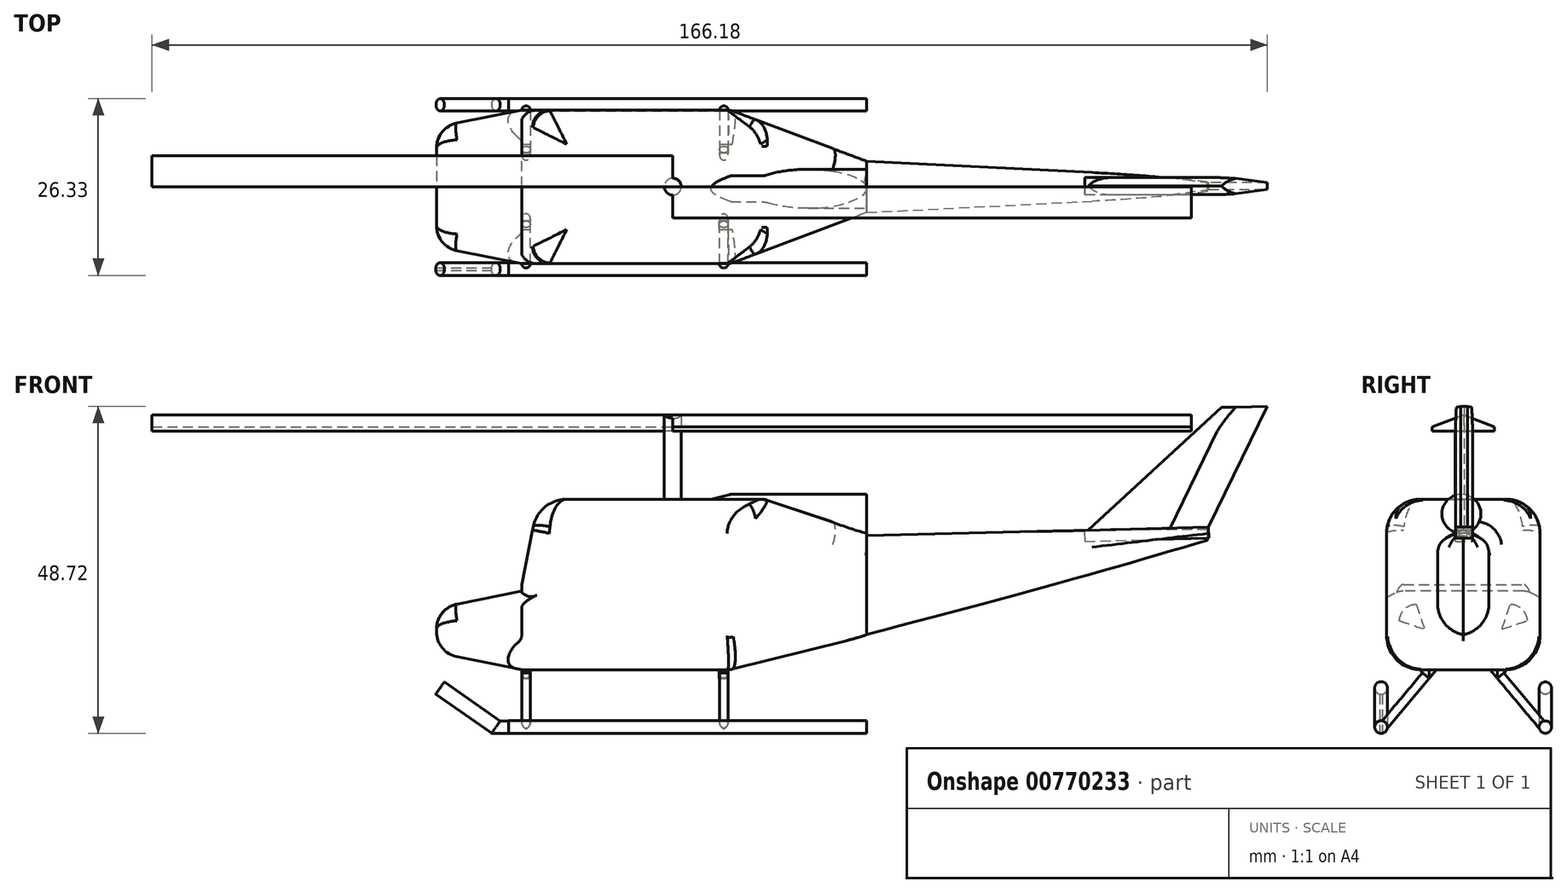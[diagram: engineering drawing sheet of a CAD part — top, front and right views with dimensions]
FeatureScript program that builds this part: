
annotation { "Feature Type Name" : "Feature", "Feature Type Description" : "" }
export const myFeature = defineFeature(function(context is Context, id is Id, definition is map)
    precondition{}
    {
        {
            var Q0;
            Q0=qCreatedBy(makeId("Top.planeOp"),FACE);
            var sketch = newSketch(context, id + "F0", { "sketchPlane" : qUnion([Q0])});
            skLineSegment(sketch, "E0.bottom", {"start": v(0, 0) * mm, "end": v(51.4, 0) * mm});
            skLineSegment(sketch, "E0.top", {"start": v(0, -22.87) * mm, "end": v(51.4, -22.87) * mm});
            skLineSegment(sketch, "E0.left", {"start": v(0, 0) * mm, "end": v(0, -22.87) * mm});
            skLineSegment(sketch, "E0.right", {"start": v(51.4, 0) * mm, "end": v(51.4, -22.87) * mm});
            skSolve(sketch);
        }
        {
            var Q0;
            Q0 = qSketchRegion(id + "F0", true);
            extrude(context, id + "F1", {"entities" : qUnion([Q0]), "depth" : 25.4 * mm, "offsetDistance" : 25.4 * mm});
        }
        {
            var Q0;
            Q0=makeQuery(id+"F1.opExtrude","SWEPT_FACE",FACE,{"disambiguationData":[OSD([sQuery(id+"F0.wireOp",EDGE,"E0.left")])]});
            var sketch = newSketch(context, id + "F2", { "sketchPlane" : qUnion([Q0])});
            skLineSegment(sketch, "E1.bottom", {"start": v(0, 0) * mm, "end": v(22.87, 0) * mm});
            skLineSegment(sketch, "E1.top", {"start": v(0, 11.7) * mm, "end": v(22.87, 11.7) * mm});
            skLineSegment(sketch, "E1.left", {"start": v(0, 0) * mm, "end": v(0, 11.7) * mm});
            skLineSegment(sketch, "E1.right", {"start": v(22.87, 0) * mm, "end": v(22.87, 11.7) * mm});
            skSolve(sketch);
        }
        {
            var Q0;
            Q0 = qSketchRegion(id + "F2", true);
            extrude(context, id + "F3", {"entities" : qUnion([Q0]), "operationType" : NewBodyOperationType.ADD, "depth" : 12.7 * mm, "offsetDistance" : 25.4 * mm});
        }
        {
            var Q0;
            Q0=makeQuery(id+"F1.opExtrude","CAP_EDGE",EDGE,{"disambiguationData":[OSD([sQuery(id+"F0.wireOp",EDGE,"E0.left")])],"isStart":false});
            chamfer(context, id + "F4", {"entities" : qUnion([Q0]), "chamferType" : ChamferType.TWO_OFFSETS, "width1" : 2.54 * mm, "oppositeDirection" : false, "width2" : 12.7 * mm, "tangentPropagation" : true});
        }
        {
            var Q0;
            Q0=makeQuery(id+"F3.opExtrude","CAP_EDGE",EDGE,{"disambiguationData":[OSD([sQuery(id+"F2.wireOp",EDGE,"E1.left")])],"isStart":false});
            var Q1;
            Q1=makeQuery(id+"F3.opExtrude","CAP_EDGE",EDGE,{"disambiguationData":[OSD([sQuery(id+"F2.wireOp",EDGE,"E1.top")])],"isStart":false});
            var Q2;
            Q2=makeQuery(id+"F3.opExtrude","CAP_EDGE",EDGE,{"disambiguationData":[OSD([sQuery(id+"F2.wireOp",EDGE,"E1.right")])],"isStart":false});
            var Q3;
            Q3=makeQuery(id+"F3.opExtrude","CAP_EDGE",EDGE,{"disambiguationData":[OSD([sQuery(id+"F2.wireOp",EDGE,"E1.bottom")])],"isStart":false});
            chamfer(context, id + "F5", {"entities" : qUnion([Q0, Q1, Q2, Q3]), "chamferType" : ChamferType.TWO_OFFSETS, "width1" : 2.54 * mm, "oppositeDirection" : false, "width2" : 12.7 * mm, "tangentPropagation" : true});
        }
        {
            var Q0;
            Q0=makeQuery(id+"F1.opExtrude","CAP_EDGE",EDGE,{"disambiguationData":[OSD([sQuery(id+"F0.wireOp",EDGE,"E0.right")])],"isStart":true});
            chamfer(context, id + "F6", {"entities" : qUnion([Q0]), "chamferType" : ChamferType.TWO_OFFSETS, "width1" : 20.32 * mm, "oppositeDirection" : false, "width2" : 5.08 * mm, "tangentPropagation" : true});
        }
        {
            var Q0;
            Q0=makeQuery(id+"F1.opExtrude","SWEPT_EDGE",EDGE,{"disambiguationData":[OSD([sQuery(id+"F0.wireOp",EDGE,"E0.top"),sQuery(id+"F0.wireOp",EDGE,"E0.right")])]});
            var Q1;
            Q1=makeQuery(id+"F1.opExtrude","SWEPT_EDGE",EDGE,{"disambiguationData":[OSD([sQuery(id+"F0.wireOp",EDGE,"E0.bottom"),sQuery(id+"F0.wireOp",EDGE,"E0.right")])]});
            chamfer(context, id + "F7", {"entities" : qUnion([Q0, Q1]), "chamferType" : ChamferType.TWO_OFFSETS, "width1" : 7.62 * mm, "oppositeDirection" : false, "width2" : 20.32 * mm, "tangentPropagation" : true});
        }
        {
            var Q0;
            Q0=makeQuery(id+"F1.opExtrude","CAP_EDGE",EDGE,{"disambiguationData":[OSD([sQuery(id+"F0.wireOp",EDGE,"E0.right")])],"isStart":false});
            chamfer(context, id + "F8", {"entities" : qUnion([Q0]), "chamferType" : ChamferType.TWO_OFFSETS, "width1" : 5.08 * mm, "oppositeDirection" : false, "width2" : 15.24 * mm, "tangentPropagation" : true});
        }
        {
            var Q0;
            Q0=makeQuery(id+"F1.opExtrude","SWEPT_FACE",FACE,{"disambiguationData":[OSD([sQuery(id+"F0.wireOp",EDGE,"E0.right")])]});
            var sketch = newSketch(context, id + "F9", { "sketchPlane" : qUnion([Q0])});
            skCircle(sketch, "E2", {"center": v(-11.72, 23.22) * mm, "radius": 2.9 * mm});
            skSolve(sketch);
        }
        {
            var Q0;
            Q0 = qSketchRegion(id + "F9", true);
            extrude(context, id + "F10", {"entities" : qUnion([Q0]), "operationType" : NewBodyOperationType.ADD, "depth" : -25.4 * mm, "offsetDistance" : 25.4 * mm});
        }
        {
            var Q0;
            Q0=makeQuery(id+"F10.opExtrude","CAP_EDGE",EDGE,{"disambiguationData":[OSD([sQuery(id+"F9.wireOp",EDGE,"E2")])],"isStart":false});
            chamfer(context, id + "F11", {"entities" : qUnion([Q0]), "chamferType" : ChamferType.TWO_OFFSETS, "width1" : 5.08 * mm, "oppositeDirection" : false, "width2" : 1.27 * mm, "tangentPropagation" : true});
        }
        {
            var Q0;
            {var subQ0=sQuery(id+"F9.wireOp",EDGE,"E2");Q0=makeQuery(id+"F11.opChamfer","BLEND_EDGE",EDGE,{"blendedFrom":[makeQuery(id+"F10.opExtrude","CAP_EDGE",EDGE,{"disambiguationData":[OSD([subQ0])],"isStart":false}),makeQuery(id+"F10.opExtrude","SWEPT_FACE",FACE,{"disambiguationData":[OSD([subQ0])]})],"blendedInto":[makeQuery(id+"F10.opExtrude","SWEPT_FACE",FACE,{"disambiguationData":[OSD([subQ0])]})]});}
            var Q1;
            {var subQ0=sQuery(id+"F9.wireOp",EDGE,"E2");Q1=makeQuery(id+"F11.opChamfer","BLEND_EDGE",EDGE,{"blendedFrom":[makeQuery(id+"F10.opExtrude","CAP_EDGE",EDGE,{"disambiguationData":[OSD([subQ0])],"isStart":false}),makeQuery(id+"F10.opExtrude","CAP_FACE",FACE,{"disambiguationData":[OSD([subQ0])],"isStart":false})],"blendedInto":[makeQuery(id+"F10.opExtrude","CAP_FACE",FACE,{"disambiguationData":[OSD([subQ0])],"isStart":false})]});}
            fillet(context, id + "F12", {"entities" : qUnion([Q0, Q1]), "radius" : 0.76 * mm, "tangentPropagation" : true, "allowEdgeOverflow" : false});
        }
        {
            var Q0;
            {var subQ0=sQuery(id+"F0.wireOp",EDGE,"E0.right");Q0=makeQuery(id+"F7.opChamfer","BLEND_EDGE",EDGE,{"blendedFrom":[makeQuery(id+"F1.opExtrude","SWEPT_EDGE",EDGE,{"disambiguationData":[OSD([sQuery(id+"F0.wireOp",EDGE,"E0.bottom"),subQ0])]}),makeQuery(id+"F6.opChamfer","BLEND_FACE",FACE,{"disambiguationData":[OSD([subQ0])]})],"blendedInto":[makeQuery(id+"F6.opChamfer","BLEND_FACE",FACE,{"disambiguationData":[OSD([subQ0])]})]});}
            var Q1;
            {var subQ0=sQuery(id+"F0.wireOp",EDGE,"E0.right");var subQ1=sQuery(id+"F0.wireOp",EDGE,"E0.bottom");Q1=makeQuery(id+"F7.opChamfer","BLEND_EDGE",EDGE,{"blendedFrom":[makeQuery(id+"F1.opExtrude","SWEPT_EDGE",EDGE,{"disambiguationData":[OSD([subQ1,subQ0])]}),makeQuery(id+"F3.boolean.opBoolean","MERGE",FACE,{"derivedFrom":[makeQuery(id+"F1.opExtrude","CAP_FACE",FACE,{"disambiguationData":[OSD([subQ1,sQuery(id+"F0.wireOp",EDGE,"E0.top"),sQuery(id+"F0.wireOp",EDGE,"E0.left"),subQ0])],"isStart":true}),makeQuery(id+"F3.opExtrude","SWEPT_FACE",FACE,{"disambiguationData":[OSD([sQuery(id+"F2.wireOp",EDGE,"E1.bottom")])]})]})],"blendedInto":[makeQuery(id+"F3.boolean.opBoolean","MERGE",FACE,{"derivedFrom":[makeQuery(id+"F1.opExtrude","CAP_FACE",FACE,{"disambiguationData":[OSD([subQ1,sQuery(id+"F0.wireOp",EDGE,"E0.top"),sQuery(id+"F0.wireOp",EDGE,"E0.left"),subQ0])],"isStart":true}),makeQuery(id+"F3.opExtrude","SWEPT_FACE",FACE,{"disambiguationData":[OSD([sQuery(id+"F2.wireOp",EDGE,"E1.bottom")])]})]})]});}
            var Q2;
            Q2=makeQuery(id+"F3.boolean.opBoolean","MERGE",EDGE,{"derivedFrom":[makeQuery(id+"F1.opExtrude","CAP_EDGE",EDGE,{"disambiguationData":[OSD([sQuery(id+"F0.wireOp",EDGE,"E0.bottom")])],"isStart":true}),makeQuery(id+"F3.opExtrude","SWEPT_EDGE",EDGE,{"disambiguationData":[OSD([sQuery(id+"F2.wireOp",EDGE,"E1.bottom"),sQuery(id+"F2.wireOp",EDGE,"E1.left")])]})]});
            var Q3;
            Q3=makeQuery(id+"F3.boolean.opBoolean","MERGE",EDGE,{"derivedFrom":[makeQuery(id+"F1.opExtrude","CAP_EDGE",EDGE,{"disambiguationData":[OSD([sQuery(id+"F0.wireOp",EDGE,"E0.top")])],"isStart":true}),makeQuery(id+"F3.opExtrude","SWEPT_EDGE",EDGE,{"disambiguationData":[OSD([sQuery(id+"F2.wireOp",EDGE,"E1.bottom"),sQuery(id+"F2.wireOp",EDGE,"E1.right")])]})]});
            var Q4;
            {var subQ0=sQuery(id+"F0.wireOp",EDGE,"E0.right");var subQ1=sQuery(id+"F0.wireOp",EDGE,"E0.top");Q4=makeQuery(id+"F7.opChamfer","BLEND_EDGE",EDGE,{"blendedFrom":[makeQuery(id+"F1.opExtrude","SWEPT_EDGE",EDGE,{"disambiguationData":[OSD([subQ1,subQ0])]}),makeQuery(id+"F3.boolean.opBoolean","MERGE",FACE,{"derivedFrom":[makeQuery(id+"F1.opExtrude","CAP_FACE",FACE,{"disambiguationData":[OSD([sQuery(id+"F0.wireOp",EDGE,"E0.bottom"),subQ1,sQuery(id+"F0.wireOp",EDGE,"E0.left"),subQ0])],"isStart":true}),makeQuery(id+"F3.opExtrude","SWEPT_FACE",FACE,{"disambiguationData":[OSD([sQuery(id+"F2.wireOp",EDGE,"E1.bottom")])]})]})],"blendedInto":[makeQuery(id+"F3.boolean.opBoolean","MERGE",FACE,{"derivedFrom":[makeQuery(id+"F1.opExtrude","CAP_FACE",FACE,{"disambiguationData":[OSD([sQuery(id+"F0.wireOp",EDGE,"E0.bottom"),subQ1,sQuery(id+"F0.wireOp",EDGE,"E0.left"),subQ0])],"isStart":true}),makeQuery(id+"F3.opExtrude","SWEPT_FACE",FACE,{"disambiguationData":[OSD([sQuery(id+"F2.wireOp",EDGE,"E1.bottom")])]})]})]});}
            var Q5;
            {var subQ0=sQuery(id+"F0.wireOp",EDGE,"E0.right");Q5=makeQuery(id+"F7.opChamfer","BLEND_EDGE",EDGE,{"blendedFrom":[makeQuery(id+"F1.opExtrude","SWEPT_EDGE",EDGE,{"disambiguationData":[OSD([sQuery(id+"F0.wireOp",EDGE,"E0.top"),subQ0])]}),makeQuery(id+"F6.opChamfer","BLEND_FACE",FACE,{"disambiguationData":[OSD([subQ0])]})],"blendedInto":[makeQuery(id+"F6.opChamfer","BLEND_FACE",FACE,{"disambiguationData":[OSD([subQ0])]})]});}
            fillet(context, id + "F13", {"entities" : qUnion([Q0, Q1, Q2, Q3, Q4, Q5]), "radius" : 5.08 * mm, "tangentPropagation" : true, "allowEdgeOverflow" : false});
        }
        {
            var Q0;
            {var subQ0=sQuery(id+"F2.wireOp",EDGE,"E1.top");Q0=makeQuery(id+"F5.opChamfer","BLEND_EDGE",EDGE,{"blendedFrom":[makeQuery(id+"F3.opExtrude","CAP_EDGE",EDGE,{"disambiguationData":[OSD([subQ0])],"isStart":false}),makeQuery(id+"F3.opExtrude","CAP_FACE",FACE,{"disambiguationData":[OSD([sQuery(id+"F2.wireOp",EDGE,"E1.bottom"),subQ0,sQuery(id+"F2.wireOp",EDGE,"E1.left"),sQuery(id+"F2.wireOp",EDGE,"E1.right")])],"isStart":false})],"blendedInto":[makeQuery(id+"F3.opExtrude","CAP_FACE",FACE,{"disambiguationData":[OSD([sQuery(id+"F2.wireOp",EDGE,"E1.bottom"),subQ0,sQuery(id+"F2.wireOp",EDGE,"E1.left"),sQuery(id+"F2.wireOp",EDGE,"E1.right")])],"isStart":false})]});}
            var Q1;
            {var subQ0=sQuery(id+"F2.wireOp",EDGE,"E1.right");Q1=makeQuery(id+"F5.opChamfer","BLEND_EDGE",EDGE,{"blendedFrom":[makeQuery(id+"F3.opExtrude","CAP_EDGE",EDGE,{"disambiguationData":[OSD([subQ0])],"isStart":false}),makeQuery(id+"F3.opExtrude","CAP_FACE",FACE,{"disambiguationData":[OSD([sQuery(id+"F2.wireOp",EDGE,"E1.bottom"),sQuery(id+"F2.wireOp",EDGE,"E1.top"),sQuery(id+"F2.wireOp",EDGE,"E1.left"),subQ0])],"isStart":false})],"blendedInto":[makeQuery(id+"F3.opExtrude","CAP_FACE",FACE,{"disambiguationData":[OSD([sQuery(id+"F2.wireOp",EDGE,"E1.bottom"),sQuery(id+"F2.wireOp",EDGE,"E1.top"),sQuery(id+"F2.wireOp",EDGE,"E1.left"),subQ0])],"isStart":false})]});}
            var Q2;
            {var subQ0=sQuery(id+"F2.wireOp",EDGE,"E1.bottom");Q2=makeQuery(id+"F5.opChamfer","BLEND_EDGE",EDGE,{"blendedFrom":[makeQuery(id+"F3.opExtrude","CAP_EDGE",EDGE,{"disambiguationData":[OSD([subQ0])],"isStart":false}),makeQuery(id+"F3.opExtrude","CAP_FACE",FACE,{"disambiguationData":[OSD([subQ0,sQuery(id+"F2.wireOp",EDGE,"E1.top"),sQuery(id+"F2.wireOp",EDGE,"E1.left"),sQuery(id+"F2.wireOp",EDGE,"E1.right")])],"isStart":false})],"blendedInto":[makeQuery(id+"F3.opExtrude","CAP_FACE",FACE,{"disambiguationData":[OSD([subQ0,sQuery(id+"F2.wireOp",EDGE,"E1.top"),sQuery(id+"F2.wireOp",EDGE,"E1.left"),sQuery(id+"F2.wireOp",EDGE,"E1.right")])],"isStart":false})]});}
            var Q3;
            {var subQ0=sQuery(id+"F2.wireOp",EDGE,"E1.left");Q3=makeQuery(id+"F5.opChamfer","BLEND_EDGE",EDGE,{"blendedFrom":[makeQuery(id+"F3.opExtrude","CAP_EDGE",EDGE,{"disambiguationData":[OSD([subQ0])],"isStart":false}),makeQuery(id+"F3.opExtrude","CAP_FACE",FACE,{"disambiguationData":[OSD([sQuery(id+"F2.wireOp",EDGE,"E1.bottom"),sQuery(id+"F2.wireOp",EDGE,"E1.top"),subQ0,sQuery(id+"F2.wireOp",EDGE,"E1.right")])],"isStart":false})],"blendedInto":[makeQuery(id+"F3.opExtrude","CAP_FACE",FACE,{"disambiguationData":[OSD([sQuery(id+"F2.wireOp",EDGE,"E1.bottom"),sQuery(id+"F2.wireOp",EDGE,"E1.top"),subQ0,sQuery(id+"F2.wireOp",EDGE,"E1.right")])],"isStart":false})]});}
            var Q4;
            Q4=makeQuery(id+"F5.opChamfer","BLEND_EDGE",EDGE,{"blendedFrom":[makeQuery(id+"F3.opExtrude","CAP_EDGE",EDGE,{"disambiguationData":[OSD([sQuery(id+"F2.wireOp",EDGE,"E1.bottom")])],"isStart":false}),makeQuery(id+"F3.opExtrude","CAP_EDGE",EDGE,{"disambiguationData":[OSD([sQuery(id+"F2.wireOp",EDGE,"E1.left")])],"isStart":false})],"blendedInto":[]});
            var Q5;
            Q5=makeQuery(id+"F5.opChamfer","BLEND_EDGE",EDGE,{"blendedFrom":[makeQuery(id+"F3.opExtrude","CAP_EDGE",EDGE,{"disambiguationData":[OSD([sQuery(id+"F2.wireOp",EDGE,"E1.bottom")])],"isStart":false}),makeQuery(id+"F3.opExtrude","CAP_EDGE",EDGE,{"disambiguationData":[OSD([sQuery(id+"F2.wireOp",EDGE,"E1.right")])],"isStart":false})],"blendedInto":[]});
            fillet(context, id + "F14", {"entities" : qUnion([Q0, Q1, Q2, Q3, Q4, Q5]), "radius" : 3.8 * mm, "tangentPropagation" : true, "allowEdgeOverflow" : false});
        }
        {
            var Q0;
            Q0=makeQuery(id+"F5.opChamfer","BLEND_EDGE",EDGE,{"blendedFrom":[makeQuery(id+"F3.opExtrude","CAP_EDGE",EDGE,{"disambiguationData":[OSD([sQuery(id+"F2.wireOp",EDGE,"E1.top")])],"isStart":false}),makeQuery(id+"F3.opExtrude","CAP_EDGE",EDGE,{"disambiguationData":[OSD([sQuery(id+"F2.wireOp",EDGE,"E1.left")])],"isStart":false})],"blendedInto":[]});
            var Q1;
            Q1=makeQuery(id+"F5.opChamfer","BLEND_EDGE",EDGE,{"blendedFrom":[makeQuery(id+"F3.opExtrude","CAP_EDGE",EDGE,{"disambiguationData":[OSD([sQuery(id+"F2.wireOp",EDGE,"E1.top")])],"isStart":false}),makeQuery(id+"F3.opExtrude","CAP_EDGE",EDGE,{"disambiguationData":[OSD([sQuery(id+"F2.wireOp",EDGE,"E1.right")])],"isStart":false})],"blendedInto":[]});
            fillet(context, id + "F15", {"entities" : qUnion([Q0, Q1]), "radius" : 2.54 * mm, "tangentPropagation" : true, "allowEdgeOverflow" : false});
        }
        {
            var Q0;
            Q0=makeQuery(id+"F4.opChamfer","BLEND_EDGE",EDGE,{"blendedFrom":[makeQuery(id+"F1.opExtrude","CAP_EDGE",EDGE,{"disambiguationData":[OSD([sQuery(id+"F0.wireOp",EDGE,"E0.left")])],"isStart":false}),makeQuery(id+"F3.boolean.opBoolean","MERGE",FACE,{"derivedFrom":[makeQuery(id+"F1.opExtrude","SWEPT_FACE",FACE,{"disambiguationData":[OSD([sQuery(id+"F0.wireOp",EDGE,"E0.bottom")])]}),makeQuery(id+"F3.opExtrude","SWEPT_FACE",FACE,{"disambiguationData":[OSD([sQuery(id+"F2.wireOp",EDGE,"E1.left")])]})]})],"blendedInto":[makeQuery(id+"F3.boolean.opBoolean","MERGE",FACE,{"derivedFrom":[makeQuery(id+"F1.opExtrude","SWEPT_FACE",FACE,{"disambiguationData":[OSD([sQuery(id+"F0.wireOp",EDGE,"E0.bottom")])]}),makeQuery(id+"F3.opExtrude","SWEPT_FACE",FACE,{"disambiguationData":[OSD([sQuery(id+"F2.wireOp",EDGE,"E1.left")])]})]})]});
            var Q1;
            Q1=makeQuery(id+"F4.opChamfer","BLEND_EDGE",EDGE,{"blendedFrom":[makeQuery(id+"F1.opExtrude","CAP_EDGE",EDGE,{"disambiguationData":[OSD([sQuery(id+"F0.wireOp",EDGE,"E0.left")])],"isStart":false}),makeQuery(id+"F3.boolean.opBoolean","MERGE",FACE,{"derivedFrom":[makeQuery(id+"F1.opExtrude","SWEPT_FACE",FACE,{"disambiguationData":[OSD([sQuery(id+"F0.wireOp",EDGE,"E0.top")])]}),makeQuery(id+"F3.opExtrude","SWEPT_FACE",FACE,{"disambiguationData":[OSD([sQuery(id+"F2.wireOp",EDGE,"E1.right")])]})]})],"blendedInto":[makeQuery(id+"F3.boolean.opBoolean","MERGE",FACE,{"derivedFrom":[makeQuery(id+"F1.opExtrude","SWEPT_FACE",FACE,{"disambiguationData":[OSD([sQuery(id+"F0.wireOp",EDGE,"E0.top")])]}),makeQuery(id+"F3.opExtrude","SWEPT_FACE",FACE,{"disambiguationData":[OSD([sQuery(id+"F2.wireOp",EDGE,"E1.right")])]})]})]});
            fillet(context, id + "F16", {"entities" : qUnion([Q0, Q1]), "radius" : 2.54 * mm, "tangentPropagation" : true, "allowEdgeOverflow" : false});
        }
        {
            var Q0;
            {var subQ0=sQuery(id+"F0.wireOp",EDGE,"E0.left");Q0=makeQuery(id+"F4.opChamfer","BLEND_EDGE",EDGE,{"blendedFrom":[makeQuery(id+"F1.opExtrude","CAP_EDGE",EDGE,{"disambiguationData":[OSD([subQ0])],"isStart":false}),makeQuery(id+"F1.opExtrude","CAP_FACE",FACE,{"disambiguationData":[OSD([sQuery(id+"F0.wireOp",EDGE,"E0.bottom"),sQuery(id+"F0.wireOp",EDGE,"E0.top"),subQ0,sQuery(id+"F0.wireOp",EDGE,"E0.right")])],"isStart":false})],"blendedInto":[makeQuery(id+"F1.opExtrude","CAP_FACE",FACE,{"disambiguationData":[OSD([sQuery(id+"F0.wireOp",EDGE,"E0.bottom"),sQuery(id+"F0.wireOp",EDGE,"E0.top"),subQ0,sQuery(id+"F0.wireOp",EDGE,"E0.right")])],"isStart":false})]});}
            fillet(context, id + "F17", {"entities" : qUnion([Q0]), "radius" : 5.08 * mm, "tangentPropagation" : true, "allowEdgeOverflow" : false});
        }
        {
            var Q0;
            {var subQ0=sQuery(id+"F0.wireOp",EDGE,"E0.right");Q0=makeQuery(id+"F8.opChamfer","BLEND_EDGE",EDGE,{"blendedFrom":[makeQuery(id+"F1.opExtrude","CAP_EDGE",EDGE,{"disambiguationData":[OSD([subQ0])],"isStart":false}),makeQuery(id+"F7.opChamfer","BLEND_FACE",FACE,{"disambiguationData":[OSD([sQuery(id+"F0.wireOp",EDGE,"E0.bottom"),subQ0])]})],"blendedInto":[makeQuery(id+"F7.opChamfer","BLEND_FACE",FACE,{"disambiguationData":[OSD([sQuery(id+"F0.wireOp",EDGE,"E0.bottom"),subQ0])]})]});}
            var Q1;
            {var subQ0=sQuery(id+"F0.wireOp",EDGE,"E0.right");Q1=makeQuery(id+"F8.opChamfer","BLEND_EDGE",EDGE,{"blendedFrom":[makeQuery(id+"F1.opExtrude","CAP_EDGE",EDGE,{"disambiguationData":[OSD([subQ0])],"isStart":false}),makeQuery(id+"F7.opChamfer","BLEND_FACE",FACE,{"disambiguationData":[OSD([sQuery(id+"F0.wireOp",EDGE,"E0.top"),subQ0])]})],"blendedInto":[makeQuery(id+"F7.opChamfer","BLEND_FACE",FACE,{"disambiguationData":[OSD([sQuery(id+"F0.wireOp",EDGE,"E0.top"),subQ0])]})]});}
            fillet(context, id + "F18", {"entities" : qUnion([Q0, Q1]), "radius" : 3.56 * mm, "tangentPropagation" : true, "allowEdgeOverflow" : false});
        }
        {
            var Q0;
            {var subQ0=sQuery(id+"F0.wireOp",EDGE,"E0.right");var subQ1=sQuery(id+"F0.wireOp",EDGE,"E0.bottom");var subQ2=makeQuery(id+"F1.opExtrude","CAP_FACE",FACE,{"disambiguationData":[OSD([subQ1,sQuery(id+"F0.wireOp",EDGE,"E0.top"),sQuery(id+"F0.wireOp",EDGE,"E0.left"),subQ0])],"isStart":false});Q0=makeQuery(id+"F10.boolean.opBoolean","SPLIT",EDGE,{"disambiguationData":[TD([makeQuery(id+"F7.opChamfer","BLEND_FACE",FACE,{"disambiguationData":[OSD([subQ1,subQ0])]})])],"derivedFrom":makeQuery(id+"F8.opChamfer","BLEND_EDGE",EDGE,{"blendedFrom":[makeQuery(id+"F1.opExtrude","CAP_EDGE",EDGE,{"disambiguationData":[OSD([subQ0])],"isStart":false}),subQ2],"blendedInto":[subQ2]})});}
            var Q1;
            {var subQ0=sQuery(id+"F0.wireOp",EDGE,"E0.right");var subQ1=sQuery(id+"F0.wireOp",EDGE,"E0.top");var subQ2=makeQuery(id+"F1.opExtrude","CAP_FACE",FACE,{"disambiguationData":[OSD([sQuery(id+"F0.wireOp",EDGE,"E0.bottom"),subQ1,sQuery(id+"F0.wireOp",EDGE,"E0.left"),subQ0])],"isStart":false});Q1=makeQuery(id+"F10.boolean.opBoolean","SPLIT",EDGE,{"disambiguationData":[TD([makeQuery(id+"F7.opChamfer","BLEND_FACE",FACE,{"disambiguationData":[OSD([subQ1,subQ0])]})])],"derivedFrom":makeQuery(id+"F8.opChamfer","BLEND_EDGE",EDGE,{"blendedFrom":[makeQuery(id+"F1.opExtrude","CAP_EDGE",EDGE,{"disambiguationData":[OSD([subQ0])],"isStart":false}),subQ2],"blendedInto":[subQ2]})});}
            fillet(context, id + "F19", {"entities" : qUnion([Q0, Q1]), "radius" : 2.54 * mm, "tangentPropagation" : true, "allowEdgeOverflow" : false});
        }
        {
            var Q0;
            Q0=makeQuery(id+"F1.opExtrude","SWEPT_FACE",FACE,{"disambiguationData":[OSD([sQuery(id+"F0.wireOp",EDGE,"E0.right")])]});
            var sketch = newSketch(context, id + "F20", { "sketchPlane" : qUnion([Q0])});
            skLineSegment(sketch, "E3.bottom", {"start": v(-7.62, 5.2) * mm, "end": v(-15.25, 5.2) * mm});
            skLineSegment(sketch, "E3.top", {"start": v(-7.62, 21.22) * mm, "end": v(-15.25, 21.22) * mm});
            skLineSegment(sketch, "E3.left", {"start": v(-7.62, 5.2) * mm, "end": v(-7.62, 21.22) * mm});
            skLineSegment(sketch, "E3.right", {"start": v(-15.25, 5.2) * mm, "end": v(-15.25, 21.22) * mm});
            skSolve(sketch);
        }
        {
            var Q0;
            Q0 = qSketchRegion(id + "F20", true);
            extrude(context, id + "F21", {"entities" : qUnion([Q0]), "depth" : 50.8 * mm, "offsetDistance" : 25.4 * mm});
        }
        {
            var Q0;
            Q0=makeQuery(id+"F21.opExtrude","CAP_EDGE",EDGE,{"disambiguationData":[OSD([sQuery(id+"F20.wireOp",EDGE,"E3.bottom")])],"isStart":false});
            chamfer(context, id + "F22", {"entities" : qUnion([Q0]), "chamferType" : ChamferType.TWO_OFFSETS, "width1" : 50.8 * mm, "oppositeDirection" : false, "width2" : 12.7 * mm, "tangentPropagation" : true});
        }
        {
            var Q0;
            Q0=makeQuery(id+"F21.opExtrude","CAP_EDGE",EDGE,{"disambiguationData":[OSD([sQuery(id+"F20.wireOp",EDGE,"E3.top")])],"isStart":true});
            chamfer(context, id + "F23", {"entities" : qUnion([Q0]), "chamferType" : ChamferType.TWO_OFFSETS, "width1" : 50.8 * mm, "oppositeDirection" : false, "width2" : 1.27 * mm, "tangentPropagation" : true});
        }
        {
            var Q0;
            Q0=makeQuery(id+"F21.opExtrude","CAP_EDGE",EDGE,{"disambiguationData":[OSD([sQuery(id+"F20.wireOp",EDGE,"E3.right")])],"isStart":false});
            var Q1;
            Q1=makeQuery(id+"F21.opExtrude","CAP_EDGE",EDGE,{"disambiguationData":[OSD([sQuery(id+"F20.wireOp",EDGE,"E3.left")])],"isStart":false});
            chamfer(context, id + "F24", {"entities" : qUnion([Q0, Q1]), "chamferType" : ChamferType.TWO_OFFSETS, "width1" : 50.8 * mm, "oppositeDirection" : false, "width2" : 2.54 * mm, "tangentPropagation" : true});
        }
        {
            var Q0;
            Q0=makeQuery(id+"F24.opChamfer","BLEND_EDGE",EDGE,{"blendedFrom":[makeQuery(id+"F21.opExtrude","CAP_EDGE",EDGE,{"disambiguationData":[OSD([sQuery(id+"F20.wireOp",EDGE,"E3.right")])],"isStart":false}),makeQuery(id+"F23.opChamfer","BLEND_FACE",FACE,{"disambiguationData":[OSD([sQuery(id+"F20.wireOp",EDGE,"E3.top")])]})],"blendedInto":[makeQuery(id+"F23.opChamfer","BLEND_FACE",FACE,{"disambiguationData":[OSD([sQuery(id+"F20.wireOp",EDGE,"E3.top")])]})]});
            var Q1;
            Q1=makeQuery(id+"F24.opChamfer","BLEND_EDGE",EDGE,{"blendedFrom":[makeQuery(id+"F21.opExtrude","CAP_EDGE",EDGE,{"disambiguationData":[OSD([sQuery(id+"F20.wireOp",EDGE,"E3.left")])],"isStart":false}),makeQuery(id+"F23.opChamfer","BLEND_FACE",FACE,{"disambiguationData":[OSD([sQuery(id+"F20.wireOp",EDGE,"E3.top")])]})],"blendedInto":[makeQuery(id+"F23.opChamfer","BLEND_FACE",FACE,{"disambiguationData":[OSD([sQuery(id+"F20.wireOp",EDGE,"E3.top")])]})]});
            fillet(context, id + "F25", {"entities" : qUnion([Q0, Q1]), "radius" : 2.54 * mm, "tangentPropagation" : true, "allowEdgeOverflow" : false});
        }
        {
            var Q0;
            Q0=makeQuery(id+"F24.opChamfer","BLEND_EDGE",EDGE,{"blendedFrom":[makeQuery(id+"F21.opExtrude","CAP_EDGE",EDGE,{"disambiguationData":[OSD([sQuery(id+"F20.wireOp",EDGE,"E3.right")])],"isStart":false}),makeQuery(id+"F22.opChamfer","BLEND_FACE",FACE,{"disambiguationData":[OSD([sQuery(id+"F20.wireOp",EDGE,"E3.bottom")])]})],"blendedInto":[makeQuery(id+"F22.opChamfer","BLEND_FACE",FACE,{"disambiguationData":[OSD([sQuery(id+"F20.wireOp",EDGE,"E3.bottom")])]})]});
            var Q1;
            Q1=makeQuery(id+"F24.opChamfer","BLEND_EDGE",EDGE,{"blendedFrom":[makeQuery(id+"F21.opExtrude","CAP_EDGE",EDGE,{"disambiguationData":[OSD([sQuery(id+"F20.wireOp",EDGE,"E3.left")])],"isStart":false}),makeQuery(id+"F22.opChamfer","BLEND_FACE",FACE,{"disambiguationData":[OSD([sQuery(id+"F20.wireOp",EDGE,"E3.bottom")])]})],"blendedInto":[makeQuery(id+"F22.opChamfer","BLEND_FACE",FACE,{"disambiguationData":[OSD([sQuery(id+"F20.wireOp",EDGE,"E3.bottom")])]})]});
            fillet(context, id + "F26", {"entities" : qUnion([Q0, Q1]), "radius" : 4.57 * mm, "tangentPropagation" : true, "allowEdgeOverflow" : false});
        }
        {
            var Q0;
            Q0=makeQuery(id+"F23.opChamfer","BLEND_FACE",FACE,{"disambiguationData":[OSD([sQuery(id+"F20.wireOp",EDGE,"E3.top")])]});
            var sketch = newSketch(context, id + "F27", { "sketchPlane" : qUnion([Q0])});
            skLineSegment(sketch, "E4.bottom", {"start": v(84.4, -12.6) * mm, "end": v(113.37, -12.6) * mm});
            skLineSegment(sketch, "E4.top", {"start": v(84.4, -10.05) * mm, "end": v(113.37, -10.05) * mm});
            skLineSegment(sketch, "E4.left", {"start": v(84.4, -12.6) * mm, "end": v(84.4, -10.05) * mm});
            skLineSegment(sketch, "E4.right", {"start": v(113.37, -12.6) * mm, "end": v(113.37, -10.05) * mm});
            skSolve(sketch);
        }
        {
            var Q0;
            Q0 = qSketchRegion(id + "F27", true);
            extrude(context, id + "F28", {"entities" : qUnion([Q0]), "depth" : 17.78 * mm, "offsetDistance" : 25.4 * mm});
        }
        {
            var Q0;
            Q0=makeQuery(id+"F28.opExtrude","CAP_EDGE",EDGE,{"disambiguationData":[OSD([sQuery(id+"F27.wireOp",EDGE,"E4.right")])],"isStart":true});
            chamfer(context, id + "F29", {"entities" : qUnion([Q0]), "chamferType" : ChamferType.TWO_OFFSETS, "width1" : 20.32 * mm, "oppositeDirection" : false, "width2" : 10.54 * mm, "tangentPropagation" : true});
        }
        {
            var Q0;
            Q0=makeQuery(id+"F28.opExtrude","CAP_EDGE",EDGE,{"disambiguationData":[OSD([sQuery(id+"F27.wireOp",EDGE,"E4.left")])],"isStart":false});
            chamfer(context, id + "F30", {"entities" : qUnion([Q0]), "chamferType" : ChamferType.TWO_OFFSETS, "width1" : 17.78 * mm, "oppositeDirection" : false, "width2" : 20.32 * mm, "tangentPropagation" : true});
        }
        {
            var Q0;
            Q0=makeQuery(id+"F28.opExtrude","CAP_FACE",FACE,{"disambiguationData":[OSD([sQuery(id+"F27.wireOp",EDGE,"E4.bottom"),sQuery(id+"F27.wireOp",EDGE,"E4.top"),sQuery(id+"F27.wireOp",EDGE,"E4.left"),sQuery(id+"F27.wireOp",EDGE,"E4.right")])],"isStart":true});
            extrude(context, id + "F31", {"entities" : qUnion([Q0]), "depth" : 1.65 * mm, "offsetDistance" : 25.4 * mm});
        }
        {
            var Q0;
            Q0=makeQuery(id+"F30.opChamfer","BLEND_EDGE",EDGE,{"blendedFrom":[makeQuery(id+"F28.opExtrude","CAP_EDGE",EDGE,{"disambiguationData":[OSD([sQuery(id+"F27.wireOp",EDGE,"E4.left")])],"isStart":false}),makeQuery(id+"F28.opExtrude","SWEPT_FACE",FACE,{"disambiguationData":[OSD([sQuery(id+"F27.wireOp",EDGE,"E4.top")])]})],"blendedInto":[makeQuery(id+"F28.opExtrude","SWEPT_FACE",FACE,{"disambiguationData":[OSD([sQuery(id+"F27.wireOp",EDGE,"E4.top")])]})]});
            var Q1;
            Q1=makeQuery(id+"F30.opChamfer","BLEND_EDGE",EDGE,{"blendedFrom":[makeQuery(id+"F28.opExtrude","CAP_EDGE",EDGE,{"disambiguationData":[OSD([sQuery(id+"F27.wireOp",EDGE,"E4.left")])],"isStart":false}),makeQuery(id+"F28.opExtrude","SWEPT_FACE",FACE,{"disambiguationData":[OSD([sQuery(id+"F27.wireOp",EDGE,"E4.bottom")])]})],"blendedInto":[makeQuery(id+"F28.opExtrude","SWEPT_FACE",FACE,{"disambiguationData":[OSD([sQuery(id+"F27.wireOp",EDGE,"E4.bottom")])]})]});
            fillet(context, id + "F32", {"entities" : qUnion([Q0, Q1]), "radius" : 2.54 * mm, "tangentPropagation" : true, "allowEdgeOverflow" : false});
        }
        {
            var Q0;
            Q0=makeQuery(id+"F29.opChamfer","BLEND_EDGE",EDGE,{"blendedFrom":[makeQuery(id+"F28.opExtrude","CAP_EDGE",EDGE,{"disambiguationData":[OSD([sQuery(id+"F27.wireOp",EDGE,"E4.right")])],"isStart":true}),makeQuery(id+"F28.opExtrude","SWEPT_FACE",FACE,{"disambiguationData":[OSD([sQuery(id+"F27.wireOp",EDGE,"E4.bottom")])]})],"blendedInto":[makeQuery(id+"F28.opExtrude","SWEPT_FACE",FACE,{"disambiguationData":[OSD([sQuery(id+"F27.wireOp",EDGE,"E4.bottom")])]})]});
            var Q1;
            Q1=makeQuery(id+"F29.opChamfer","BLEND_EDGE",EDGE,{"blendedFrom":[makeQuery(id+"F28.opExtrude","CAP_EDGE",EDGE,{"disambiguationData":[OSD([sQuery(id+"F27.wireOp",EDGE,"E4.right")])],"isStart":true}),makeQuery(id+"F28.opExtrude","SWEPT_FACE",FACE,{"disambiguationData":[OSD([sQuery(id+"F27.wireOp",EDGE,"E4.top")])]})],"blendedInto":[makeQuery(id+"F28.opExtrude","SWEPT_FACE",FACE,{"disambiguationData":[OSD([sQuery(id+"F27.wireOp",EDGE,"E4.top")])]})]});
            chamfer(context, id + "F33", {"entities" : qUnion([Q0, Q1]), "chamferType" : ChamferType.TWO_OFFSETS, "width1" : 5.08 * mm, "oppositeDirection" : false, "width2" : 0.76 * mm, "tangentPropagation" : true});
        }
        {
            var Q0;
            Q0=makeQuery(id+"F1.opExtrude","CAP_FACE",FACE,{"disambiguationData":[OSD([sQuery(id+"F0.wireOp",EDGE,"E0.bottom"),sQuery(id+"F0.wireOp",EDGE,"E0.top"),sQuery(id+"F0.wireOp",EDGE,"E0.left"),sQuery(id+"F0.wireOp",EDGE,"E0.right")])],"isStart":false});
            var sketch = newSketch(context, id + "F34", { "sketchPlane" : qUnion([Q0])});
            skCircle(sketch, "E5", {"center": v(22.51, -11.4) * mm, "radius": 1.26 * mm});
            skSolve(sketch);
        }
        {
            var Q0;
            Q0 = qSketchRegion(id + "F34", true);
            extrude(context, id + "F35", {"entities" : qUnion([Q0]), "operationType" : NewBodyOperationType.ADD, "depth" : 12.7 * mm, "offsetDistance" : 25.4 * mm});
        }
        {
            var Q0;
            Q0=makeQuery(id+"F3.boolean.opBoolean","MERGE",FACE,{"derivedFrom":[makeQuery(id+"F1.opExtrude","CAP_FACE",FACE,{"disambiguationData":[OSD([sQuery(id+"F0.wireOp",EDGE,"E0.bottom"),sQuery(id+"F0.wireOp",EDGE,"E0.top"),sQuery(id+"F0.wireOp",EDGE,"E0.left"),sQuery(id+"F0.wireOp",EDGE,"E0.right")])],"isStart":true}),makeQuery(id+"F3.opExtrude","SWEPT_FACE",FACE,{"disambiguationData":[OSD([sQuery(id+"F2.wireOp",EDGE,"E1.bottom")])]})]});
            var sketch = newSketch(context, id + "F36", { "sketchPlane" : qUnion([Q0])});
            skLineSegment(sketch, "E6.bottom", {"start": v(0, 17.8) * mm, "end": v(1.3, 17.8) * mm});
            skLineSegment(sketch, "E6.top", {"start": v(0, 16.5) * mm, "end": v(1.3, 16.5) * mm});
            skLineSegment(sketch, "E6.left", {"start": v(0, 17.8) * mm, "end": v(0, 16.5) * mm});
            skLineSegment(sketch, "E6.right", {"start": v(1.3, 17.8) * mm, "end": v(1.3, 16.5) * mm});
            skLineSegment(sketch, "E7.bottom", {"start": v(0, 5.08) * mm, "end": v(1.3, 5.08) * mm});
            skLineSegment(sketch, "E7.top", {"start": v(0, 6.38) * mm, "end": v(1.3, 6.38) * mm});
            skLineSegment(sketch, "E7.left", {"start": v(0, 5.08) * mm, "end": v(0, 6.38) * mm});
            skLineSegment(sketch, "E7.right", {"start": v(1.3, 5.08) * mm, "end": v(1.3, 6.38) * mm});
            skLineSegment(sketch, "E8.bottom", {"start": v(30.76, 17.8) * mm, "end": v(29.4, 17.8) * mm});
            skLineSegment(sketch, "E8.top", {"start": v(30.76, 16.5) * mm, "end": v(29.4, 16.5) * mm});
            skLineSegment(sketch, "E8.left", {"start": v(30.76, 17.8) * mm, "end": v(30.76, 16.5) * mm});
            skLineSegment(sketch, "E8.right", {"start": v(29.4, 17.8) * mm, "end": v(29.4, 16.5) * mm});
            skLineSegment(sketch, "E9.bottom", {"start": v(30.76, 5.08) * mm, "end": v(29.47, 5.08) * mm});
            skLineSegment(sketch, "E9.top", {"start": v(30.76, 6.39) * mm, "end": v(29.47, 6.39) * mm});
            skLineSegment(sketch, "E9.left", {"start": v(30.76, 5.08) * mm, "end": v(30.76, 6.39) * mm});
            skLineSegment(sketch, "E9.right", {"start": v(29.47, 5.08) * mm, "end": v(29.47, 6.39) * mm});
            skSolve(sketch);
        }
        {
            var Q0;
            Q0 = qSketchRegion(id + "F36", true);
            extrude(context, id + "F37", {"entities" : qUnion([Q0]), "operationType" : NewBodyOperationType.ADD, "depth" : 1.3 * mm, "offsetDistance" : 25.4 * mm});
        }
        {
            var Q0;
            Q0=makeQuery(id+"F37.opExtrude","CAP_EDGE",EDGE,{"disambiguationData":[OSD([sQuery(id+"F36.wireOp",EDGE,"E6.bottom")])],"isStart":false});
            var Q1;
            Q1=makeQuery(id+"F37.opExtrude","CAP_EDGE",EDGE,{"disambiguationData":[OSD([sQuery(id+"F36.wireOp",EDGE,"E8.bottom")])],"isStart":false});
            var Q2;
            Q2=makeQuery(id+"F37.opExtrude","CAP_EDGE",EDGE,{"disambiguationData":[OSD([sQuery(id+"F36.wireOp",EDGE,"E7.bottom")])],"isStart":false});
            var Q3;
            Q3=makeQuery(id+"F37.opExtrude","CAP_EDGE",EDGE,{"disambiguationData":[OSD([sQuery(id+"F36.wireOp",EDGE,"E9.bottom")])],"isStart":false});
            chamfer(context, id + "F38", {"entities" : qUnion([Q0, Q1, Q2, Q3]), "chamferType" : ChamferType.OFFSET_ANGLE, "width" : 1.3 * mm, "oppositeDirection" : false, "angle" : 40 * degree, "tangentPropagation" : true});
        }
        {
            var Q0;
            Q0=makeQuery(id+"F38.opChamfer","BLEND_FACE",FACE,{"disambiguationData":[OSD([sQuery(id+"F36.wireOp",EDGE,"E7.bottom")])]});
            var sketch = newSketch(context, id + "F39", { "sketchPlane" : qUnion([Q0])});
            skCircle(sketch, "E10", {"center": v(0.65, 5.07) * mm, "radius": 0.64 * mm});
            skPoint(sketch, "E10.centerSnap0", {"position": v(0.65, 4.03) * mm});
            skCircle(sketch, "E11", {"center": v(30.11, 5.07) * mm, "radius": 0.64 * mm});
            skPoint(sketch, "E11.centerSnap0", {"position": v(30.11, 4.7) * mm});
            skSolve(sketch);
        }
        {
            var Q0;
            Q0 = qSketchRegion(id + "F39", true);
            extrude(context, id + "F40", {"entities" : qUnion([Q0]), "operationType" : NewBodyOperationType.ADD, "depth" : 10.16 * mm, "offsetDistance" : 25.4 * mm});
        }
        {
            var Q0;
            Q0 = qSketchRegion(id + "F39", true);
            extrude(context, id + "F41", {"entities" : qUnion([Q0]), "operationType" : NewBodyOperationType.ADD, "depth" : -2.54 * mm, "offsetDistance" : 25.4 * mm});
        }
        {
            var Q0;
            Q0=makeQuery(id+"F38.opChamfer","BLEND_FACE",FACE,{"disambiguationData":[OSD([sQuery(id+"F36.wireOp",EDGE,"E8.bottom")])]});
            var sketch = newSketch(context, id + "F42", { "sketchPlane" : qUnion([Q0])});
            skCircle(sketch, "E12", {"center": v(30.1, 12.48) * mm, "radius": 0.65 * mm});
            skCircle(sketch, "E13", {"center": v(0.65, 12.47) * mm, "radius": 0.65 * mm});
            skSolve(sketch);
        }
        {
            var Q0;
            Q0 = qSketchRegion(id + "F42", true);
            extrude(context, id + "F43", {"entities" : qUnion([Q0]), "operationType" : NewBodyOperationType.ADD, "depth" : 10.16 * mm, "offsetDistance" : 25.4 * mm});
        }
        {
            var Q0;
            Q0 = qSketchRegion(id + "F42", true);
            extrude(context, id + "F44", {"entities" : qUnion([Q0]), "operationType" : NewBodyOperationType.ADD, "depth" : -2.54 * mm, "offsetDistance" : 25.4 * mm});
        }
        {
            var Q0;
            Q0=makeQuery(id+"F10.opExtrude","CAP_FACE",FACE,{"disambiguationData":[OSD([sQuery(id+"F9.wireOp",EDGE,"E2")])],"isStart":true});
            var sketch = newSketch(context, id + "F45", { "sketchPlane" : qUnion([Q0])});
            skCircle(sketch, "E14", {"center": v(-23.68, -8.55) * mm, "radius": 0.94 * mm});
            skCircle(sketch, "E15", {"center": v(0.8, -8.55) * mm, "radius": 0.92 * mm});
            skSolve(sketch);
        }
        {
            var Q0;
            Q0 = qSketchRegion(id + "F45", true);
            extrude(context, id + "F46", {"entities" : qUnion([Q0]), "operationType" : NewBodyOperationType.ADD, "depth" : -53.34 * mm, "offsetDistance" : 25.4 * mm});
        }
        {
            var Q0;
            Q0=makeQuery(id+"F46.opExtrude","CAP_FACE",FACE,{"disambiguationData":[OSD([sQuery(id+"F45.wireOp",EDGE,"E14")])],"isStart":false});
            var sketch = newSketch(context, id + "F47", { "sketchPlane" : qUnion([Q0])});
            skLineSegment(sketch, "E16.bottom", {"start": v(22.75, -9.48) * mm, "end": v(24.62, -9.48) * mm});
            skLineSegment(sketch, "E16.top", {"start": v(22.75, -7.62) * mm, "end": v(24.62, -7.62) * mm});
            skLineSegment(sketch, "E16.left", {"start": v(22.75, -9.48) * mm, "end": v(22.75, -7.62) * mm});
            skLineSegment(sketch, "E16.right", {"start": v(24.62, -9.48) * mm, "end": v(24.62, -7.62) * mm});
            skLineSegment(sketch, "E17.bottom", {"start": v(-1.7, -9.45) * mm, "end": v(0.11, -9.45) * mm});
            skLineSegment(sketch, "E17.top", {"start": v(-1.7, -7.65) * mm, "end": v(0.11, -7.65) * mm});
            skLineSegment(sketch, "E17.left", {"start": v(-1.7, -9.45) * mm, "end": v(-1.7, -7.65) * mm});
            skLineSegment(sketch, "E17.right", {"start": v(0.11, -9.45) * mm, "end": v(0.11, -7.65) * mm});
            skSolve(sketch);
        }
        {
            var Q0;
            Q0 = qSketchRegion(id + "F47", true);
            extrude(context, id + "F48", {"entities" : qUnion([Q0]), "operationType" : NewBodyOperationType.ADD, "depth" : 2.54 * mm, "offsetDistance" : 25.4 * mm});
        }
        {
            var Q0;
            Q0=makeQuery(id+"F48.opExtrude","CAP_EDGE",EDGE,{"disambiguationData":[OSD([sQuery(id+"F47.wireOp",EDGE,"E16.top")])],"isStart":false});
            var Q1;
            Q1=makeQuery(id+"F48.opExtrude","CAP_EDGE",EDGE,{"disambiguationData":[OSD([sQuery(id+"F47.wireOp",EDGE,"E17.top")])],"isStart":false});
            chamfer(context, id + "F49", {"entities" : qUnion([Q0, Q1]), "chamferType" : ChamferType.OFFSET_ANGLE, "width" : 1.3 * mm, "oppositeDirection" : false, "angle" : 55 * degree, "tangentPropagation" : true});
        }
        {
            var Q0;
            Q0=makeQuery(id+"F48.opExtrude","SWEPT_EDGE",EDGE,{"disambiguationData":[OSD([sQuery(id+"F47.wireOp",EDGE,"E17.top"),sQuery(id+"F47.wireOp",EDGE,"E17.left")])]});
            var Q1;
            Q1=makeQuery(id+"F48.opExtrude","SWEPT_EDGE",EDGE,{"disambiguationData":[OSD([sQuery(id+"F47.wireOp",EDGE,"E17.top"),sQuery(id+"F47.wireOp",EDGE,"E17.right")])]});
            var Q2;
            Q2=makeQuery(id+"F48.opExtrude","SWEPT_EDGE",EDGE,{"disambiguationData":[OSD([sQuery(id+"F47.wireOp",EDGE,"E17.bottom"),sQuery(id+"F47.wireOp",EDGE,"E17.right")])]});
            var Q3;
            Q3=makeQuery(id+"F48.opExtrude","SWEPT_EDGE",EDGE,{"disambiguationData":[OSD([sQuery(id+"F47.wireOp",EDGE,"E17.bottom"),sQuery(id+"F47.wireOp",EDGE,"E17.left")])]});
            var Q4;
            Q4=makeQuery(id+"F48.opExtrude","SWEPT_EDGE",EDGE,{"disambiguationData":[OSD([sQuery(id+"F47.wireOp",EDGE,"E16.bottom"),sQuery(id+"F47.wireOp",EDGE,"E16.right")])]});
            var Q5;
            Q5=makeQuery(id+"F48.opExtrude","SWEPT_EDGE",EDGE,{"disambiguationData":[OSD([sQuery(id+"F47.wireOp",EDGE,"E16.bottom"),sQuery(id+"F47.wireOp",EDGE,"E16.left")])]});
            var Q6;
            Q6=makeQuery(id+"F48.opExtrude","SWEPT_EDGE",EDGE,{"disambiguationData":[OSD([sQuery(id+"F47.wireOp",EDGE,"E16.top"),sQuery(id+"F47.wireOp",EDGE,"E16.right")])]});
            var Q7;
            Q7=makeQuery(id+"F48.opExtrude","SWEPT_EDGE",EDGE,{"disambiguationData":[OSD([sQuery(id+"F47.wireOp",EDGE,"E16.top"),sQuery(id+"F47.wireOp",EDGE,"E16.left")])]});
            fillet(context, id + "F50", {"entities" : qUnion([Q0, Q1, Q2, Q3, Q4, Q5, Q6, Q7]), "radius" : 0.89 * mm, "tangentPropagation" : true, "allowEdgeOverflow" : false});
        }
        {
            var Q0;
            Q0=makeQuery(id+"F49.opChamfer","BLEND_FACE",FACE,{"disambiguationData":[OSD([sQuery(id+"F47.wireOp",EDGE,"E16.top")])]});
            var Q1;
            Q1=makeQuery(id+"F49.opChamfer","BLEND_FACE",FACE,{"disambiguationData":[OSD([sQuery(id+"F47.wireOp",EDGE,"E17.top")])]});
            extrude(context, id + "F51", {"entities" : qUnion([Q0, Q1]), "operationType" : NewBodyOperationType.ADD, "depth" : 10.16 * mm, "offsetDistance" : 25.4 * mm});
        }
        {
            var Q0;
            {var subQ0=sQuery(id+"F47.wireOp",EDGE,"E16.right");var subQ1=sQuery(id+"F47.wireOp",EDGE,"E16.left");var subQ2=sQuery(id+"F47.wireOp",EDGE,"E16.top");var subQ3=sQuery(id+"F47.wireOp",EDGE,"E16.bottom");Q0=makeQuery(id+"F51.boolean.opBoolean","MERGE",EDGE,{"derivedFrom":[makeQuery(id+"F49.opChamfer","BLEND_EDGE",EDGE,{"blendedFrom":[makeQuery(id+"F48.opExtrude","CAP_EDGE",EDGE,{"disambiguationData":[OSD([subQ2])],"isStart":false}),makeQuery(id+"F48.opExtrude","CAP_FACE",FACE,{"disambiguationData":[OSD([subQ3,subQ2,subQ1,subQ0])],"isStart":false})],"blendedInto":[makeQuery(id+"F48.opExtrude","CAP_FACE",FACE,{"disambiguationData":[OSD([subQ3,subQ2,subQ1,subQ0])],"isStart":false})]}),makeQuery(id+"F51.opExtrude","CAP_EDGE",EDGE,{"disambiguationData":[OSD([subQ3,subQ2,subQ1,subQ0])],"isStart":true})]});}
            fillet(context, id + "F52", {"entities" : qUnion([Q0]), "radius" : 5.08 * mm, "tangentPropagation" : true, "allowEdgeOverflow" : false});
        }
        {
            var Q0;
            Q0=makeQuery(id+"F35.opExtrude","CAP_FACE",FACE,{"disambiguationData":[OSD([sQuery(id+"F34.wireOp",EDGE,"E5")])],"isStart":false});
            var sketch = newSketch(context, id + "F53", { "sketchPlane" : qUnion([Q0])});
            skLineSegment(sketch, "E18.bottom", {"start": v(22.51, -11.4) * mm, "end": v(99.8, -11.4) * mm});
            skLineSegment(sketch, "E18.top", {"start": v(22.51, -16.1) * mm, "end": v(99.8, -16.1) * mm});
            skLineSegment(sketch, "E18.left", {"start": v(22.51, -11.4) * mm, "end": v(22.51, -16.1) * mm});
            skLineSegment(sketch, "E18.right", {"start": v(99.8, -11.4) * mm, "end": v(99.8, -16.1) * mm});
            skLineSegment(sketch, "E19.bottom", {"start": v(22.51, -11.4) * mm, "end": v(-55.07, -11.4) * mm});
            skLineSegment(sketch, "E19.top", {"start": v(22.51, -6.8) * mm, "end": v(-55.07, -6.8) * mm});
            skLineSegment(sketch, "E19.left", {"start": v(22.51, -11.4) * mm, "end": v(22.51, -6.8) * mm});
            skLineSegment(sketch, "E19.right", {"start": v(-55.07, -11.4) * mm, "end": v(-55.07, -6.8) * mm});
            skSolve(sketch);
        }
        {
            var Q0;
            Q0 = qSketchRegion(id + "F53", true);
            extrude(context, id + "F54", {"entities" : qUnion([Q0]), "operationType" : NewBodyOperationType.ADD, "depth" : -2.54 * mm, "offsetDistance" : 25.4 * mm});
        }
        {
            var Q0;
            Q0=makeQuery(id+"F54.opExtrude","CAP_EDGE",EDGE,{"disambiguationData":[OSD([sQuery(id+"F53.wireOp",EDGE,"E19.top")])],"isStart":true});
            var Q1;
            Q1=makeQuery(id+"F54.opExtrude","CAP_EDGE",EDGE,{"disambiguationData":[OSD([sQuery(id+"F53.wireOp",EDGE,"E18.top")])],"isStart":true});
            chamfer(context, id + "F55", {"entities" : qUnion([Q0, Q1]), "chamferType" : ChamferType.TWO_OFFSETS, "width1" : 5.08 * mm, "oppositeDirection" : false, "width2" : 1.9 * mm, "tangentPropagation" : true});
        }
    });
